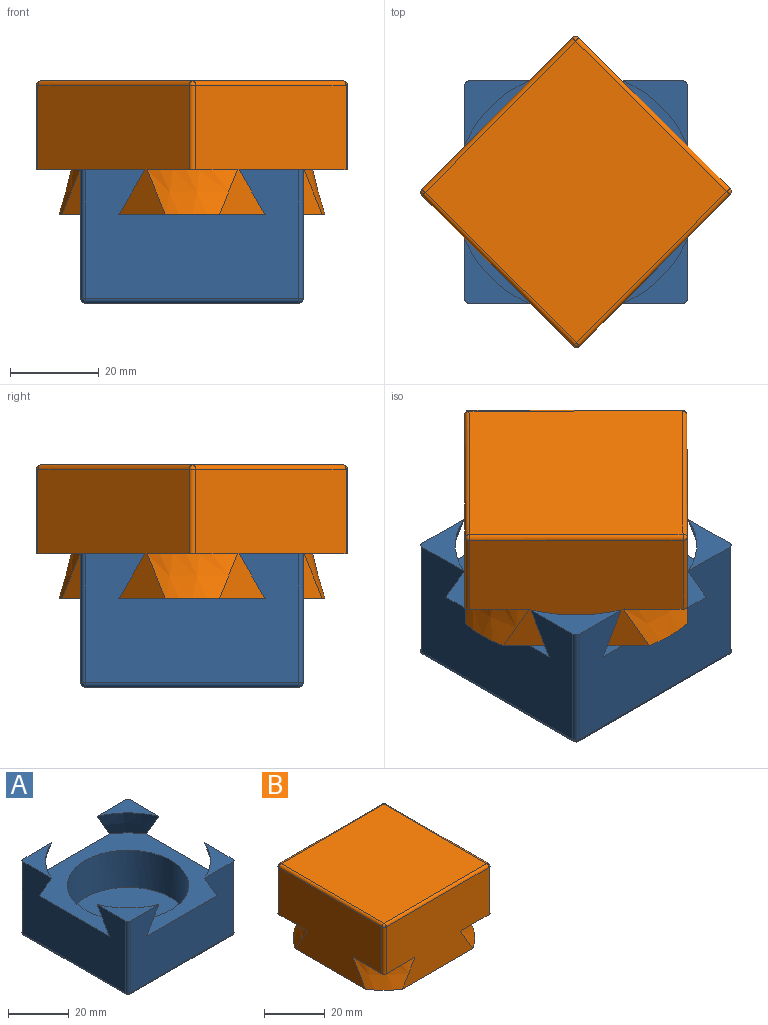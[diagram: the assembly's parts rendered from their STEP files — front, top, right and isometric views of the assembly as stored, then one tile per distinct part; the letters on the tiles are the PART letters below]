
ASSEMBLY  parts=2 mates=1
PART A: 28 faces, bbox 58.3x58.3x30 mm
  f0: plane 40x40mm, normal (0,0,1), area 1256.6mm2, adj f1
  f1: cylinder r=20mm len=40mm, axis (0,0,-1), area 1885mm2, adj f0,f2
  f2: plane 50x50mm, normal (0,0,1), area 1115.2mm2, adj f1,f3,f4,f5,f6,f8,f9,f10
  f3: revolved ~18.55x18.41mm, area 171.2mm2, adj f2,f9,f11,f15
  f4: revolved ~18.55x18.41mm, area 171.2mm2, adj f2,f9,f10,f14
  f5: revolved ~18.55x18.41mm, area 171.2mm2, adj f2,f8,f10,f13
  f6: revolved ~18.55x18.41mm, area 171.2mm2, adj f2,f8,f11,f12
  f7: plane 48x48mm, normal (0,0,-1), area 2304mm2, adj f18,f21,f24,f27
  f8: plane 48x29mm, normal (-1,0,0), area 1122.2mm2, adj f2,f5,f6,f12,f13,f22,f23,f27
  f9: plane 48x29mm, normal (1,0,0), area 1122.2mm2, adj f2,f3,f4,f14,f15,f16,f17,f18
  f10: plane 48x29mm, normal (0,1,0), area 1122.2mm2, adj f2,f4,f5,f13,f14,f16,f21,f22
  f11: plane 48x29mm, normal (0,-1,0), area 1122.2mm2, adj f2,f3,f6,f12,f15,f17,f23,f24
  f12: plane 14.39x14.39mm, normal (0,0,1), area 76.3mm2, adj f6,f8,f11,f23
  f13: plane 14.39x14.39mm, normal (0,0,1), area 76.3mm2, adj f5,f8,f10,f22
  f14: plane 14.39x14.39mm, normal (0,0,1), area 76.3mm2, adj f4,f9,f10,f16
  f15: plane 14.39x14.39mm, normal (0,0,1), area 76.3mm2, adj f3,f9,f11,f17
  f16: cylinder r=1mm len=29mm, axis (0,0,-1), area 45.6mm2, adj f9,f10,f14,f19
  f17: cylinder r=1mm len=29mm, axis (0,0,1), area 45.6mm2, adj f9,f11,f15,f20
  f18: cylinder r=1mm len=48mm, axis (0,-1,0), area 75.4mm2, adj f7,f9,f19,f20
  f19: sphere r=1mm, area 1.6mm2, adj f16,f18,f21
  f20: sphere r=1mm, area 1.6mm2, adj f17,f18,f24
  f21: cylinder r=1mm len=48mm, axis (-1,0,0), area 75.4mm2, adj f7,f10,f19,f25
  f22: cylinder r=1mm len=29mm, axis (0,0,1), area 45.6mm2, adj f8,f10,f13,f25
  f23: cylinder r=1mm len=29mm, axis (0,0,-1), area 45.6mm2, adj f8,f11,f12,f26
  f24: cylinder r=1mm len=48mm, axis (1,0,0), area 75.4mm2, adj f7,f11,f20,f26
  f25: sphere r=1mm, area 1.6mm2, adj f21,f22,f27
  f26: sphere r=1mm, area 1.6mm2, adj f23,f24,f27
  f27: cylinder r=1mm len=48mm, axis (0,1,0), area 75.4mm2, adj f7,f8,f25,f26
PART B: 28 faces, bbox 58.3x58.3x30 mm
  f0: cylinder r=20mm len=40mm, axis (0,0,-1), area 3141.6mm2, adj f1,f2
  f1: plane 40x40mm, normal (0,0,-1), area 1256.6mm2, adj f0
  f2: plane 50x50mm, normal (0,0,-1), area 1115.2mm2, adj f0,f3,f4,f5,f6,f11,f12,f14
  f3: revolved ~18.55x18.41mm, area 171.2mm2, adj f2,f13,f14,f15
  f4: revolved ~18.55x18.41mm, area 171.2mm2, adj f2,f10,f11,f15
  f5: revolved ~18.55x18.41mm, area 171.2mm2, adj f2,f9,f11,f12
  f6: revolved ~18.55x18.41mm, area 171.2mm2, adj f2,f8,f12,f14
  f7: plane 48x48mm, normal (0,0,1), area 2304mm2, adj f19,f20,f24,f25
  f8: plane 14.39x14.39mm, normal (0,0,-1), area 76.3mm2, adj f6,f12,f14,f16
  f9: plane 14.39x14.39mm, normal (0,0,-1), area 76.3mm2, adj f5,f11,f12,f21
  f10: plane 14.39x14.39mm, normal (0,0,-1), area 76.3mm2, adj f4,f11,f15,f27
  f11: plane 48x29mm, normal (0,1,0), area 1181.8mm2, adj f2,f4,f5,f9,f10,f21,f25,f27
  f12: plane 48x29mm, normal (-1,0,0), area 1181.8mm2, adj f2,f5,f6,f8,f9,f16,f20,f21
  f13: plane 14.39x14.39mm, normal (0,0,-1), area 76.3mm2, adj f3,f14,f15,f18
  f14: plane 48x29mm, normal (0,-1,0), area 1181.8mm2, adj f2,f3,f6,f8,f13,f16,f18,f19
  f15: plane 48x29mm, normal (1,0,0), area 1181.8mm2, adj f2,f3,f4,f10,f13,f18,f24,f27
  f16: cylinder r=1mm len=19mm, axis (0,0,-1), area 29.8mm2, adj f8,f12,f14,f17
  f17: sphere r=1mm, area 1.6mm2, adj f16,f19,f20
  f18: cylinder r=1mm len=19mm, axis (0,0,1), area 29.8mm2, adj f13,f14,f15,f22
  f19: cylinder r=1mm len=48mm, axis (-1,0,0), area 75.4mm2, adj f7,f14,f17,f22
  f20: cylinder r=1mm len=48mm, axis (0,-1,0), area 75.4mm2, adj f7,f12,f17,f23
  f21: cylinder r=1mm len=19mm, axis (0,0,1), area 29.8mm2, adj f9,f11,f12,f23
  f22: sphere r=1mm, area 1.6mm2, adj f18,f19,f24
  f23: sphere r=1mm, area 1.6mm2, adj f20,f21,f25
  f24: cylinder r=1mm len=48mm, axis (0,1,0), area 75.4mm2, adj f7,f15,f22,f26
  f25: cylinder r=1mm len=48mm, axis (1,0,0), area 75.4mm2, adj f7,f11,f23,f26
  f26: sphere r=1mm, area 1.6mm2, adj f24,f25,f27
  f27: cylinder r=1mm len=19mm, axis (0,0,-1), area 29.8mm2, adj f10,f11,f15,f26
PLACE A at identity fixed
PLACE B rot(axis=(0,0,1),45.2deg) t=(25.1,-10.36,0)mm
MATE revolute A.f1 <-> B.f0  axis (0,0,-1) through (25,25,20)mm
